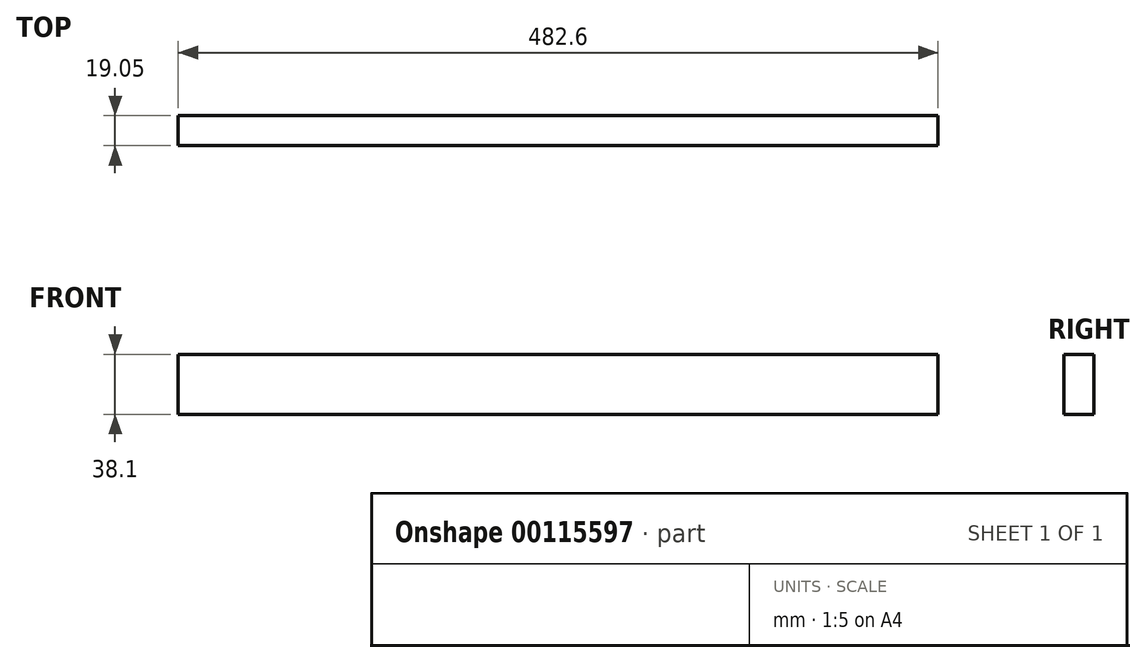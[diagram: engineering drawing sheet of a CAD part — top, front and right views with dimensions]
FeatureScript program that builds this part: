
annotation { "Feature Type Name" : "Feature", "Feature Type Description" : "" }
export const myFeature = defineFeature(function(context is Context, id is Id, definition is map)
    precondition{}
    {
        {
            var Q0;
            Q0=qCreatedBy(makeId("Front.planeOp"),FACE);
            var sketch = newSketch(context, id + "F0", { "sketchPlane" : qUnion([Q0])});
            skLineSegment(sketch, "E0.bottom", {"start": v(-241.3, 19.05) * mm, "end": v(241.3, 19.05) * mm});
            skLineSegment(sketch, "E0.top", {"start": v(-241.3, -19.05) * mm, "end": v(241.3, -19.05) * mm});
            skLineSegment(sketch, "E0.left", {"start": v(-241.3, 19.05) * mm, "end": v(-241.3, -19.05) * mm});
            skLineSegment(sketch, "E0.right", {"start": v(241.3, 19.05) * mm, "end": v(241.3, -19.05) * mm});
            skPoint(sketch, "E0.middle", {"position": v(0, 0) * mm});
            skSolve(sketch);
        }
        {
            var Q0;
            Q0=makeQuery(id+"F0.imprint","IMPRINT",FACE,{"disambiguationData":[TD([[makeQuery(id+"F0.imprint","IMPRINT",EDGE,{"derivedFrom":sQuery(id+"F0.wireOp",EDGE,"E0.bottom")}),-1.0]])]});
            extrude(context, id + "F1", {"entities" : qUnion([Q0]), "depth" : 19.05 * mm});
        }
    });
